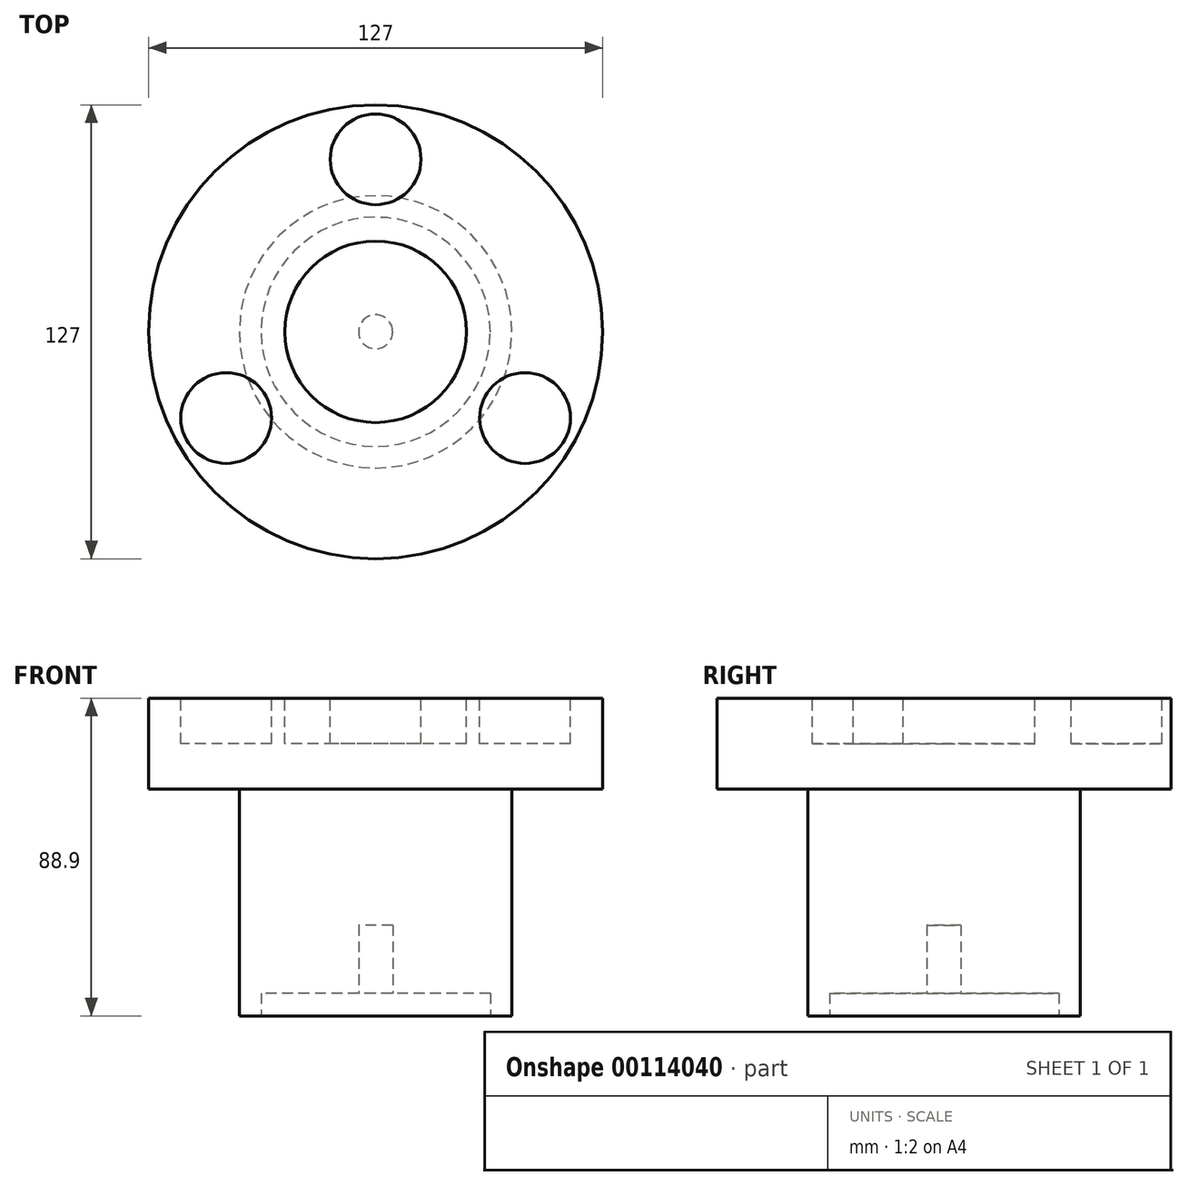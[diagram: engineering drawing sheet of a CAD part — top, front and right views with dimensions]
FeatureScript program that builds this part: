
annotation { "Feature Type Name" : "Feature", "Feature Type Description" : "" }
export const myFeature = defineFeature(function(context is Context, id is Id, definition is map)
    precondition{}
    {
        {
            var Q0;
            Q0=qCreatedBy(makeId("Top.planeOp"),FACE);
            var sketch = newSketch(context, id + "F0", { "sketchPlane" : qUnion([Q0])});
            skCircle(sketch, "E0", {"center": v(0, 0) * mm, "radius": 38.1 * mm});
            skCircle(sketch, "E1", {"center": v(0, 0) * mm, "radius": 32.07 * mm});
            skSolve(sketch);
        }
        {
            var Q0;
            Q0 = qSketchRegion(id + "F0", true);
            var Q1;
            Q1=makeQuery(id+"F0.imprint","IMPRINT",FACE,{"disambiguationData":[TD([[makeQuery(id+"F0.imprint","IMPRINT",EDGE,{"derivedFrom":sQuery(id+"F0.wireOp",EDGE,"E1")}),1.0]])]});
            extrude(context, id + "F1", {"entities" : qUnion([Q0, Q1]), "depth" : 63.5 * mm});
        }
        {
            var Q0;
            Q0=makeQuery(id+"F0.imprint","IMPRINT",FACE,{"disambiguationData":[TD([[makeQuery(id+"F0.imprint","IMPRINT",EDGE,{"derivedFrom":sQuery(id+"F0.wireOp",EDGE,"E1")}),1.0]])]});
            extrude(context, id + "F2", {"entities" : qUnion([Q0]), "operationType" : NewBodyOperationType.REMOVE, "depth" : 6.35 * mm});
        }
        {
            var Q0;
            Q0=qCreatedBy(makeId("Top.planeOp"),FACE);
            var sketch = newSketch(context, id + "F3", { "sketchPlane" : qUnion([Q0])});
            skCircle(sketch, "E2", {"center": v(0, 0) * mm, "radius": 4.76 * mm});
            skSolve(sketch);
        }
        {
            var Q0;
            Q0 = qSketchRegion(id + "F3", true);
            extrude(context, id + "F4", {"entities" : qUnion([Q0]), "operationType" : NewBodyOperationType.REMOVE, "depth" : 25.4 * mm});
        }
        {
            var Q0;
            Q0=makeQuery(id+"F1.opExtrude","CAP_FACE",FACE,{"disambiguationData":[OSD([sQuery(id+"F0.wireOp",EDGE,"E0")])],"isStart":false});
            var sketch = newSketch(context, id + "F5", { "sketchPlane" : qUnion([Q0])});
            skCircle(sketch, "E3", {"center": v(0, 0) * mm, "radius": 63.5 * mm});
            skSolve(sketch);
        }
        {
            var Q0;
            Q0 = qSketchRegion(id + "F5", true);
            extrude(context, id + "F6", {"entities" : qUnion([Q0]), "operationType" : NewBodyOperationType.ADD, "depth" : 25.4 * mm});
        }
        {
            var Q0;
            Q0=makeQuery(id+"F6.opExtrude","CAP_FACE",FACE,{"disambiguationData":[OSD([sQuery(id+"F5.wireOp",EDGE,"E3")])],"isStart":false});
            var sketch = newSketch(context, id + "F7", { "sketchPlane" : qUnion([Q0])});
            skCircle(sketch, "E4", {"center": v(0, 48.26) * mm, "radius": 12.7 * mm});
            skCircle(sketch, "E5.1.0", {"center": v(-41.8, -24.13) * mm, "radius": 12.7 * mm});
            skCircle(sketch, "E5.2.0", {"center": v(41.8, -24.13) * mm, "radius": 12.7 * mm});
            skPoint(sketch, "E5.center", {"position": v(0, 0) * mm});
            skCircle(sketch, "E6", {"center": v(0, 0) * mm, "radius": 25.4 * mm});
            skSolve(sketch);
        }
        {
            var Q0;
            Q0 = qSketchRegion(id + "F7", true);
            extrude(context, id + "F8", {"entities" : qUnion([Q0]), "operationType" : NewBodyOperationType.REMOVE, "oppositeDirection" : true, "depth" : 12.7 * mm});
        }
    });
